# Revit family: FA_КомпенсаторПолосы_75025_EZETEK
name_source: partatom
category: Системы пожарной сигнализации
revit_build: Autodesk Revit 2017 (Build: 20170118_1100(x64)
units: mm (PartAtom-declared; Revit-internal decimal feet)

## family parameters
Всегда вертикально = Да
На основе рабочей плоскости = Нет
Общий = Да
При загрузке вырезать с полостями = Нет
Размер круглого соединителя = Использовать радиус
Сохранять ориентацию аннотаций = Нет
Тип детали = Нормальный
Точка расчета площади = Нет

## types (1)
- КомпенсаторПолосы_75025
    ADSK_Версия Revit = 2017
    ADSK_Единица измерения = шт.
    ADSK_Завод-изготовитель = Ezetek
    ADSK_Код изделия = 75025
    ADSK_Количество = 1
    ADSK_Марка = 75025
    ADSK_Масса = 0.32
    ADSK_Масса_Текст = 0.32
    ADSK_Материал = BIMLIB_Сталь_Нержавеющая_EZETEK
    ADSK_Наименование = Компенсатор полосы, оцинк
    ADSK_Обозначение = 75025
    URL = https://ezetek.ru
    Группа модели = Полоса
    Изготовитель = Ezetek
    Описание = Компенсатор полосы применяется для организации системы уравнивания потенциалов на протяженных объектах. Компенсатор применяется для параллельного соединения участков полосы при конструкции зданий из независимых секций, между которыми возможны температурные колебания длины в течение года.
    Угол = 90.00°
